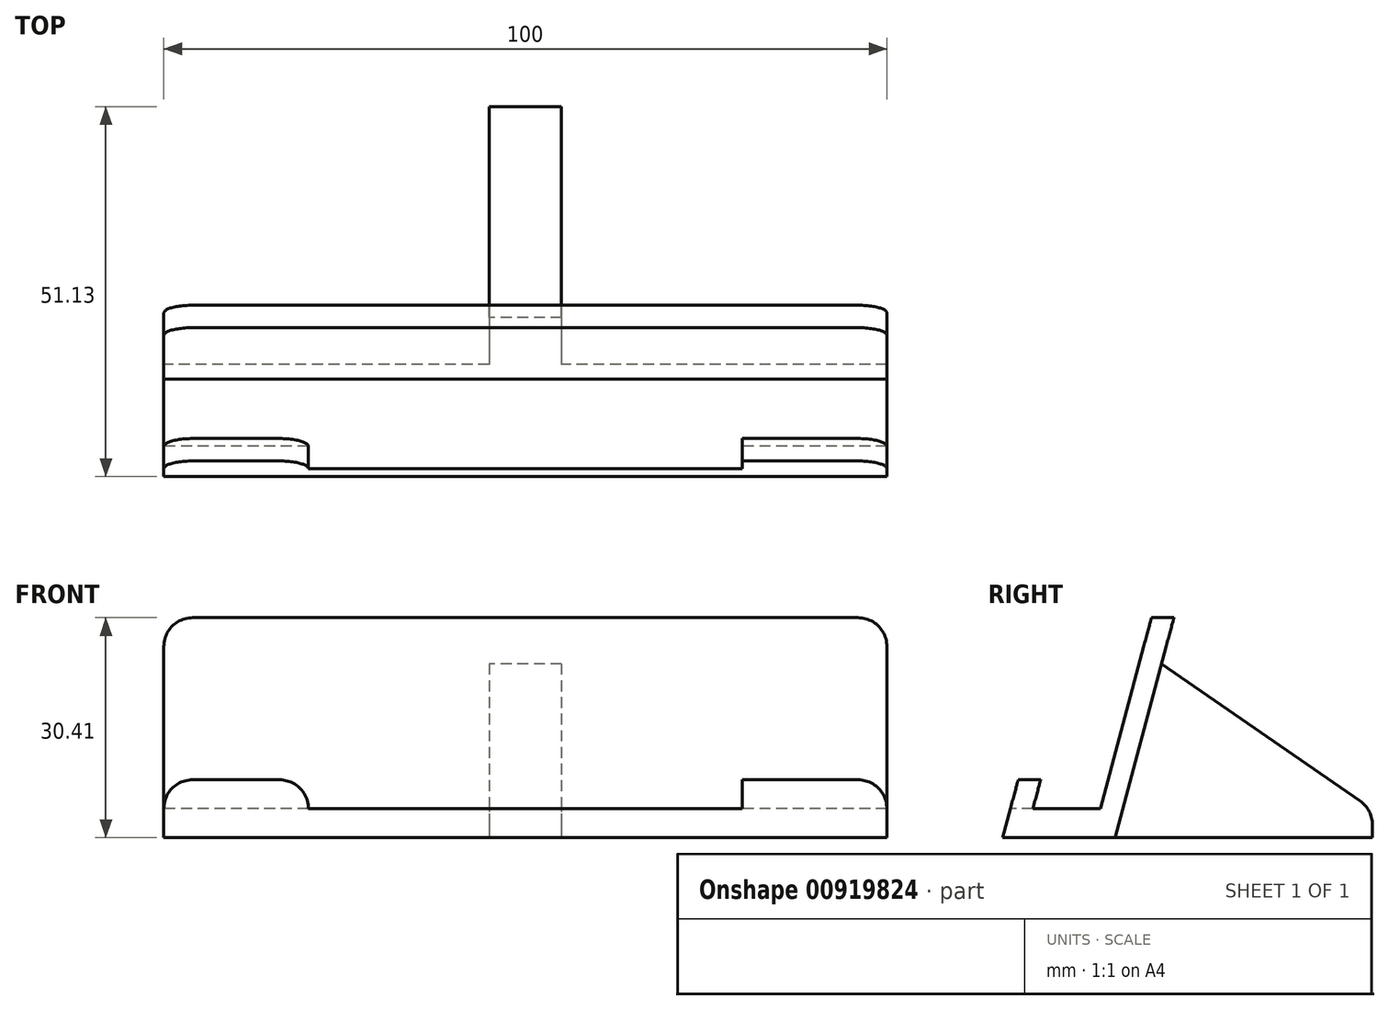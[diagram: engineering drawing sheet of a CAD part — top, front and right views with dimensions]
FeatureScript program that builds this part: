
annotation { "Feature Type Name" : "Feature", "Feature Type Description" : "" }
export const myFeature = defineFeature(function(context is Context, id is Id, definition is map)
    precondition{}
    {
        {
            var Q0;
            Q0=qCreatedBy(makeId("Right.planeOp"),FACE);
            var sketch = newSketch(context, id + "F0", { "sketchPlane" : qUnion([Q0])});
            skLineSegment(sketch, "E0", {"start": v(-8.16, 30.4) * mm, "end": v(-15.24, 4) * mm});
            skLineSegment(sketch, "E1", {"start": v(-15.24, 4) * mm, "end": v(-24.56, 4) * mm});
            skLineSegment(sketch, "E2", {"start": v(-24.56, 4) * mm, "end": v(-23.49, 8) * mm});
            skLineSegment(sketch, "E3", {"start": v(-23.49, 8) * mm, "end": v(-26.6, 8) * mm});
            skLineSegment(sketch, "E4", {"start": v(-26.6, 8) * mm, "end": v(-28.74, 0) * mm});
            skLineSegment(sketch, "E5", {"start": v(-28.74, 0) * mm, "end": v(-13.2, 0) * mm});
            skLineSegment(sketch, "E6", {"start": v(-5.06, 30.4) * mm, "end": v(-8.16, 30.4) * mm});
            skLineSegment(sketch, "E7", {"start": v(-5.06, 30.4) * mm, "end": v(-13.2, 0) * mm});
            skSolve(sketch);
        }
        {
            var Q0;
            Q0=makeQuery(id+"F0.imprint","IMPRINT",FACE,{"disambiguationData":[TD([[makeQuery(id+"F0.imprint","IMPRINT",EDGE,{"derivedFrom":sQuery(id+"F0.wireOp",EDGE,"E0")}),1.0]])]});
            extrude(context, id + "F1", {"entities" : qUnion([Q0]), "depth" : 100 * mm, "offsetDistance" : 25 * mm});
        }
        {
            var Q0;
            Q0=makeQuery(id+"F1.opExtrude","CAP_FACE",FACE,{"disambiguationData":[OSD([sQuery(id+"F0.wireOp",EDGE,"E0"),sQuery(id+"F0.wireOp",EDGE,"E1"),sQuery(id+"F0.wireOp",EDGE,"E2"),sQuery(id+"F0.wireOp",EDGE,"E3"),sQuery(id+"F0.wireOp",EDGE,"E4"),sQuery(id+"F0.wireOp",EDGE,"E5"),sQuery(id+"F0.wireOp",EDGE,"E6"),sQuery(id+"F0.wireOp",EDGE,"E7")])],"isStart":true});
            var sketch = newSketch(context, id + "F2", { "sketchPlane" : qUnion([Q0])});
            skLineSegment(sketch, "E8", {"start": v(6.77, 24.02) * mm, "end": v(-22.39, 3.88) * mm});
            skLineSegment(sketch, "E9", {"start": v(-22.39, 3.88) * mm, "end": v(-22.39, 0) * mm});
            skLineSegment(sketch, "E10", {"start": v(-22.39, 0) * mm, "end": v(13.2, 0) * mm});
            skLineSegment(sketch, "E11", {"start": v(6.77, 24.02) * mm, "end": v(13.2, 0) * mm});
            skSolve(sketch);
        }
        {
            var Q0;
            Q0 = qSketchRegion(id + "F2", true);
            extrude(context, id + "F3", {"entities" : qUnion([Q0]), "operationType" : NewBodyOperationType.ADD, "oppositeDirection" : true, "depth" : 55 * mm, "offsetDistance" : 25 * mm, "hasSecondDirection" : true, "secondDirectionOppositeDirection" : true, "secondDirectionDepth" : 45 * mm});
        }
        {
            var Q0;
            Q0=makeQuery(id+"F1.opExtrude","CAP_EDGE",EDGE,{"disambiguationData":[OSD([sQuery(id+"F0.wireOp",EDGE,"E6")])],"isStart":true});
            var Q1;
            Q1=makeQuery(id+"F1.opExtrude","CAP_EDGE",EDGE,{"disambiguationData":[OSD([sQuery(id+"F0.wireOp",EDGE,"E6")])],"isStart":false});
            var Q2;
            Q2=makeQuery(id+"F1.opExtrude","CAP_EDGE",EDGE,{"disambiguationData":[OSD([sQuery(id+"F0.wireOp",EDGE,"E3")])],"isStart":false});
            var Q3;
            Q3=makeQuery(id+"F1.opExtrude","CAP_EDGE",EDGE,{"disambiguationData":[OSD([sQuery(id+"F0.wireOp",EDGE,"E3")])],"isStart":true});
            var Q4;
            Q4=makeQuery(id+"F3.opExtrude","SWEPT_EDGE",EDGE,{"disambiguationData":[OSD([sQuery(id+"F2.wireOp",EDGE,"E8"),sQuery(id+"F2.wireOp",EDGE,"E9")])]});
            var Q5;
            Q5=makeQuery(id+"F3.opExtrude","SWEPT_EDGE",EDGE,{"disambiguationData":[OSD([sQuery(id+"F0.wireOp",EDGE,"E7"),sQuery(id+"F2.wireOp",EDGE,"E8"),sQuery(id+"F2.wireOp",EDGE,"E11")])]});
            var Q6;
            Q6=makeQuery(id+"F3.opExtrude","CAP_EDGE",EDGE,{"disambiguationData":[OSD([sQuery(id+"F2.wireOp",EDGE,"E11")])],"isStart":true});
            var Q7;
            Q7=makeQuery(id+"F3.opExtrude","CAP_EDGE",EDGE,{"disambiguationData":[OSD([sQuery(id+"F2.wireOp",EDGE,"E11")])],"isStart":false});
            fillet(context, id + "F4", {"entities" : qUnion([Q0, Q1, Q2, Q3, Q4, Q5, Q6, Q7]), "radius" : 4 * mm, "tangentPropagation" : true, "allowEdgeOverflow" : false});
        }
        {
            var Q0;
            Q0=makeQuery(id+"F1.opExtrude","SWEPT_FACE",FACE,{"disambiguationData":[OSD([sQuery(id+"F0.wireOp",EDGE,"E3")])]});
            var sketch = newSketch(context, id + "F5", { "sketchPlane" : qUnion([Q0])});
            skLineSegment(sketch, "E12.bottom", {"start": v(20, -23.49) * mm, "end": v(80, -23.49) * mm});
            skLineSegment(sketch, "E12.top", {"start": v(20, -32.16) * mm, "end": v(80, -32.16) * mm});
            skLineSegment(sketch, "E12.left", {"start": v(20, -23.49) * mm, "end": v(20, -32.16) * mm});
            skLineSegment(sketch, "E12.right", {"start": v(80, -23.49) * mm, "end": v(80, -32.16) * mm});
            skSolve(sketch);
        }
        {
            var Q0;
            Q0 = qSketchRegion(id + "F5", true);
            extrude(context, id + "F6", {"entities" : qUnion([Q0]), "operationType" : NewBodyOperationType.REMOVE, "oppositeDirection" : true, "depth" : 4 * mm, "offsetDistance" : 25 * mm});
        }
        {
            var Q0;
            Q0=makeQuery(id+"F6.boolean.opBoolean","COPY",EDGE,{"derivedFrom":makeQuery(id+"F6.opExtrude","CAP_EDGE",EDGE,{"disambiguationData":[OSD([sQuery(id+"F5.wireOp",EDGE,"E12.left")])],"isStart":true})});
            var Q1;
            Q1=makeQuery(id+"F6.boolean.opBoolean","COPY",EDGE,{"derivedFrom":makeQuery(id+"F6.opExtrude","CAP_EDGE",EDGE,{"disambiguationData":[OSD([sQuery(id+"F5.wireOp",EDGE,"E12.right")])],"isStart":true})});
            fillet(context, id + "F7", {"entities" : qUnion([Q0, Q1]), "radius" : 4 * mm, "tangentPropagation" : true, "allowEdgeOverflow" : false});
        }
    });
